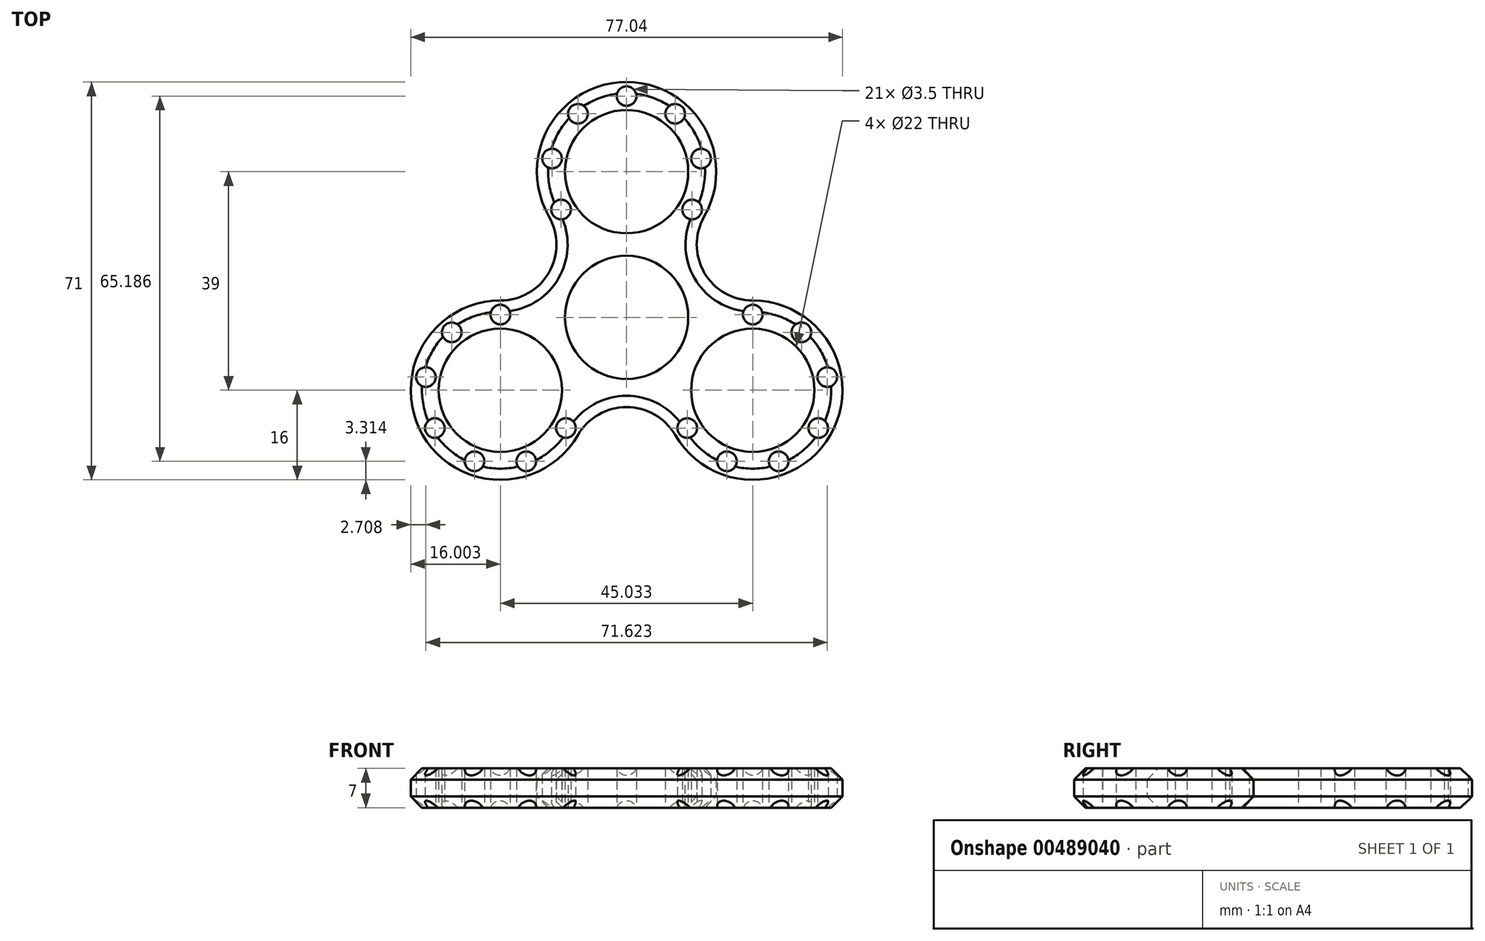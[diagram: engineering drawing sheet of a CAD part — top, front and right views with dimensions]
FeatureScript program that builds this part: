
annotation { "Feature Type Name" : "Feature", "Feature Type Description" : "" }
export const myFeature = defineFeature(function(context is Context, id is Id, definition is map)
    precondition{}
    {
        {
            var Q0;
            Q0=qCreatedBy(makeId("Top.planeOp"),FACE);
            var sketch = newSketch(context, id + "F0", { "sketchPlane" : qUnion([Q0])});
            skCircle(sketch, "E0", {"center": v(0, 0) * mm, "radius": 11 * mm});
            skCircle(sketch, "E1", {"center": v(0, 26) * mm, "radius": 11 * mm});
            skArc(sketch, "E2.0", {"start": v(13.86, 18) * mm, "mid": v(0, 42) * mm, "end": v(-13.86, 18) * mm});
            skCircle(sketch, "E3.1.0", {"center": v(-22.52, -13) * mm, "radius": 11 * mm});
            skArc(sketch, "E3.1.1", {"start": v(-22.52, 3) * mm, "mid": v(-36.37, -21) * mm, "end": v(-8.66, -21) * mm});
            skCircle(sketch, "E3.2.0", {"center": v(22.52, -13) * mm, "radius": 11 * mm});
            skArc(sketch, "E3.2.1", {"start": v(8.66, -21) * mm, "mid": v(36.37, -21) * mm, "end": v(22.52, 3) * mm});
            skArc(sketch, "E4", {"start": v(-22.52, 3) * mm, "mid": v(-13.86, 8) * mm, "end": v(-13.86, 18) * mm});
            skArc(sketch, "E5", {"start": v(13.86, 18) * mm, "mid": v(13.86, 8) * mm, "end": v(22.52, 3) * mm});
            skArc(sketch, "E6", {"start": v(-8.66, -21) * mm, "mid": v(0, -16) * mm, "end": v(8.66, -21) * mm});
            skPoint(sketch, "E7", {"position": v(-11.7, 19.25) * mm});
            skCircle(sketch, "E8", {"center": v(-11.7, 19.25) * mm, "radius": 1.75 * mm});
            skCircle(sketch, "E9.1.0", {"center": v(-13.3, 28.34) * mm, "radius": 1.75 * mm});
            skCircle(sketch, "E9.2.0", {"center": v(-8.68, 36.34) * mm, "radius": 1.75 * mm});
            skCircle(sketch, "E9.3.0", {"center": v(0, 39.5) * mm, "radius": 1.75 * mm});
            skCircle(sketch, "E9.4.0", {"center": v(8.68, 36.34) * mm, "radius": 1.75 * mm});
            skCircle(sketch, "E9.5.0", {"center": v(13.3, 28.34) * mm, "radius": 1.75 * mm});
            skCircle(sketch, "E9.6.0", {"center": v(11.7, 19.25) * mm, "radius": 1.75 * mm});
            skLineSegment(sketch, "E9.anchor2", {"start": v(10.18, 20.13) * mm, "end": v(11.7, 19.25) * mm, "construction": true});
            skLineSegment(sketch, "E10.trimOffspring", {"start": v(-11.7, 19.25) * mm, "end": v(-9.53, 20.5) * mm});
            skCircle(sketch, "E11.1.0", {"center": v(-10.83, -19.75) * mm, "radius": 1.75 * mm});
            skCircle(sketch, "E11.1.1", {"center": v(-17.9, -25.69) * mm, "radius": 1.75 * mm});
            skCircle(sketch, "E11.1.2", {"center": v(-27.13, -25.69) * mm, "radius": 1.75 * mm});
            skCircle(sketch, "E11.1.3", {"center": v(-34.2, -19.75) * mm, "radius": 1.75 * mm});
            skCircle(sketch, "E11.1.4", {"center": v(-35.81, -10.66) * mm, "radius": 1.75 * mm});
            skCircle(sketch, "E11.1.5", {"center": v(-31.2, -2.66) * mm, "radius": 1.75 * mm});
            skCircle(sketch, "E11.1.6", {"center": v(-22.52, 0.5) * mm, "radius": 1.75 * mm});
            skCircle(sketch, "E11.2.0", {"center": v(22.52, 0.5) * mm, "radius": 1.75 * mm});
            skCircle(sketch, "E11.2.1", {"center": v(31.2, -2.66) * mm, "radius": 1.75 * mm});
            skCircle(sketch, "E11.2.2", {"center": v(35.81, -10.66) * mm, "radius": 1.75 * mm});
            skCircle(sketch, "E11.2.3", {"center": v(34.2, -19.75) * mm, "radius": 1.75 * mm});
            skCircle(sketch, "E11.2.4", {"center": v(27.13, -25.69) * mm, "radius": 1.75 * mm});
            skCircle(sketch, "E11.2.5", {"center": v(17.9, -25.69) * mm, "radius": 1.75 * mm});
            skCircle(sketch, "E11.2.6", {"center": v(10.83, -19.75) * mm, "radius": 1.75 * mm});
            skLineSegment(sketch, "E12", {"start": v(-11.7, 19.25) * mm, "end": v(-10.15, 18.42) * mm});
            skLineSegment(sketch, "E13", {"start": v(10.15, 18.42) * mm, "end": v(11.7, 19.25) * mm});
            skPoint(sketch, "E14.orphan", {"position": v(0, 13) * mm});
            skPoint(sketch, "E15.orphan", {"position": v(0, 15) * mm});
            skPoint(sketch, "E16.start.orphan", {"position": v(0, 11) * mm});
            skSolve(sketch);
        }
        {
            var Q0;
            Q0=makeQuery(id+"F0.imprint","IMPRINT",FACE,{"disambiguationData":[TD([[makeQuery(id+"F0.imprint","IMPRINT",EDGE,{"derivedFrom":sQuery(id+"F0.wireOp",EDGE,"E0")}),-1.0]])]});
            extrude(context, id + "F1", {"entities" : qUnion([Q0]), "endBound" : BoundingType.SYMMETRIC, "depth" : 7 * mm});
        }
        {
            var Q0;
            Q0=makeQuery(id+"F1.opExtrude","CAP_EDGE",EDGE,{"disambiguationData":[OSD([sQuery(id+"F0.wireOp",EDGE,"E3.1.1")])],"isStart":false});
            var Q1;
            Q1=makeQuery(id+"F1.opExtrude","CAP_EDGE",EDGE,{"disambiguationData":[OSD([sQuery(id+"F0.wireOp",EDGE,"E6")])],"isStart":false});
            var Q2;
            Q2=makeQuery(id+"F1.opExtrude","CAP_EDGE",EDGE,{"disambiguationData":[OSD([sQuery(id+"F0.wireOp",EDGE,"E3.2.1")])],"isStart":false});
            var Q3;
            Q3=makeQuery(id+"F1.opExtrude","CAP_EDGE",EDGE,{"disambiguationData":[OSD([sQuery(id+"F0.wireOp",EDGE,"E5")])],"isStart":false});
            var Q4;
            Q4=makeQuery(id+"F1.opExtrude","CAP_EDGE",EDGE,{"disambiguationData":[OSD([sQuery(id+"F0.wireOp",EDGE,"E2.0")])],"isStart":false});
            var Q5;
            Q5=makeQuery(id+"F1.opExtrude","CAP_EDGE",EDGE,{"disambiguationData":[OSD([sQuery(id+"F0.wireOp",EDGE,"E4")])],"isStart":false});
            var Q6;
            Q6=makeQuery(id+"F1.opExtrude","CAP_EDGE",EDGE,{"disambiguationData":[OSD([sQuery(id+"F0.wireOp",EDGE,"E6")])],"isStart":true});
            var Q7;
            Q7=makeQuery(id+"F1.opExtrude","CAP_EDGE",EDGE,{"disambiguationData":[OSD([sQuery(id+"F0.wireOp",EDGE,"E3.1.1")])],"isStart":true});
            var Q8;
            Q8=makeQuery(id+"F1.opExtrude","CAP_EDGE",EDGE,{"disambiguationData":[OSD([sQuery(id+"F0.wireOp",EDGE,"E4")])],"isStart":true});
            var Q9;
            Q9=makeQuery(id+"F1.opExtrude","CAP_EDGE",EDGE,{"disambiguationData":[OSD([sQuery(id+"F0.wireOp",EDGE,"E2.0")])],"isStart":true});
            var Q10;
            Q10=makeQuery(id+"F1.opExtrude","CAP_EDGE",EDGE,{"disambiguationData":[OSD([sQuery(id+"F0.wireOp",EDGE,"E5")])],"isStart":true});
            var Q11;
            Q11=makeQuery(id+"F1.opExtrude","CAP_EDGE",EDGE,{"disambiguationData":[OSD([sQuery(id+"F0.wireOp",EDGE,"E3.2.1")])],"isStart":true});
            chamfer(context, id + "F2", {"entities" : qUnion([Q0, Q1, Q2, Q3, Q4, Q5, Q6, Q7, Q8, Q9, Q10, Q11]), "width" : 2 * mm, "tangentPropagation" : true});
        }
    });
